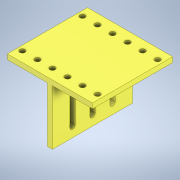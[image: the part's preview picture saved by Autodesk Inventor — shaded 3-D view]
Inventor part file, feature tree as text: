
AUTODESK INVENTOR PART (.ipt)
format: ipt  version: 2022.1 (Build 261234020, 234B)  size: 203,776 bytes
history: native  units: in
note: dims shown in document units (in); Inventor stores cm internally (conversion verified against a paired STEP export)
features: sketch x7, extrude x5, hole x2
ambient origin geometry x8: Origin, YZ Plane, XZ Plane, XY Plane, X Axis, Y Axis, Z Axis, Center Point
bodies: Solid1 (feature_tree)
feature tree (14):
  extrude  "Extrusion1"  Depth=4.0in
  extrude  "Extrusion2"  TaperAngle=0.0deg  [1 undecoded]
  extrude  "Extrusion3"  Depth=3.0in
  hole  "Hole1"  [1 undecoded]
  hole  "Hole2"  [1 undecoded]
  extrude  "Extrusion5"  Depth=0.5in
  extrude  "Extrusion6"  Depth=0.133in
  sketch  "Sketch1"  dims[d0=4.0in d1=0.8862in]
  sketch  "Sketch2"  dims[d2=0.25in d3=0.0in]
  sketch  "Sketch3"  dims[d4=0.25in d5=3.0in]
  sketch  "Sketch4"  dims[d6=0.0in d7=2.0in]
  sketch  "Sketch5"  dims[d8=2.0in d9=0.25in]
  sketch  "Sketch8"  dims[d10=0.0in d11=0.5in]
  sketch  "Sketch9"  dims[d12=1.5748in d14=1.0in d15=0.3937in d17=1.0in d19=0.201in d20=0.75in d21=0.563in d22=0.12in d23=0.5635in d24=0.281in d25=0.0in d26=1.5in d27=3.0in d28=0.25in d29=0.7874in d31=3.0in d32=2.7559in d34=0.75in d37=0.266in d38=0.75in d39=0.375in d40=0.25in d41=0.5635in d42=1.0in d43=0.0in d48=0.5in d49=0.0in d50=0.0in d51=0.5in d52=0.5in d53=1.0in d54=1.0in d55=1.0in d56=0.133in d57=0.0in d58=0.0in]
note: 3 required parameter values undecoded (feature->parameter linkage not recoverable at this tier; creation-order binding heuristic only, values carry confidence <= 0.55)
